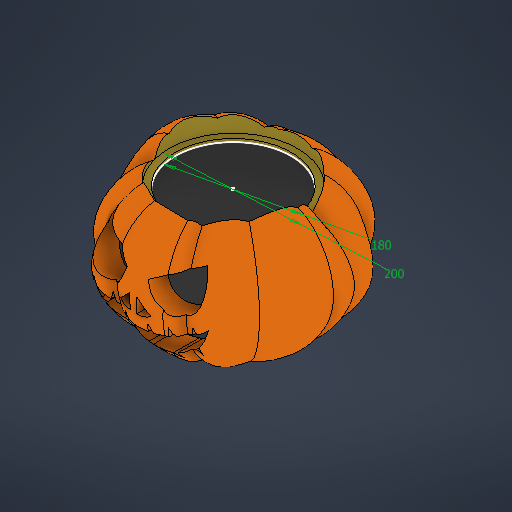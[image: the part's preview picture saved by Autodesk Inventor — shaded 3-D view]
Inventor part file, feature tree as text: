
AUTODESK INVENTOR PART (.ipt)
format: ipt  version: 2025.1 (Build 291241020, 241B)  size: 1,449,984 bytes
history: native  units: in
note: dims shown in document units (in); Inventor stores cm internally (conversion verified against a paired STEP export)
features: other x14, extrude x4, sketch x2
ambient origin geometry x8: Origin, YZ Plane, XZ Plane, XY Plane, X Axis, Y Axis, Z Axis, Center Point
bodies: Solid1 (feature_tree)
feature tree (20):
  other  "Axe1"
  other  "Plan1"
  other  "Plan2"
  other  "Plan3"
  other  "Plan4"
  other  "Plan5"
  other  "Plan6"
  other  "Plan7"
  other  "Plan8"
  other  "Plan9"
  other  "Plan10"
  other  "Plan11"
  other  "Plan12"
  extrude  "Extrusion1"  Depth=3.937in TaperAngle=0.0deg
  sketch  "Sketch3"  dims[d9=0.9781in d10=0.0in d11=7.0866in d12=7.874in d13=3.812in d14=0.0in d15=3.812in d16=0.0in d17=0.1969in d18=0.0in d3=0.0197in d4=0.0344in d5=0.0197in d6=0.0344in d7=0.0197in d8=0.0344in]
  extrude  "Extrusion3"  Depth=7.0866in
  extrude  "Extrusion4"  Depth=7.874in
  extrude  "Extrusion5"  Depth=7.874in TaperAngle=0.0deg
  sketch  "Sketch1"  dims[d0=7.874in d1=3.937in d2=0.0in]
  other  "Enlèv. mat.-Extru.2"
